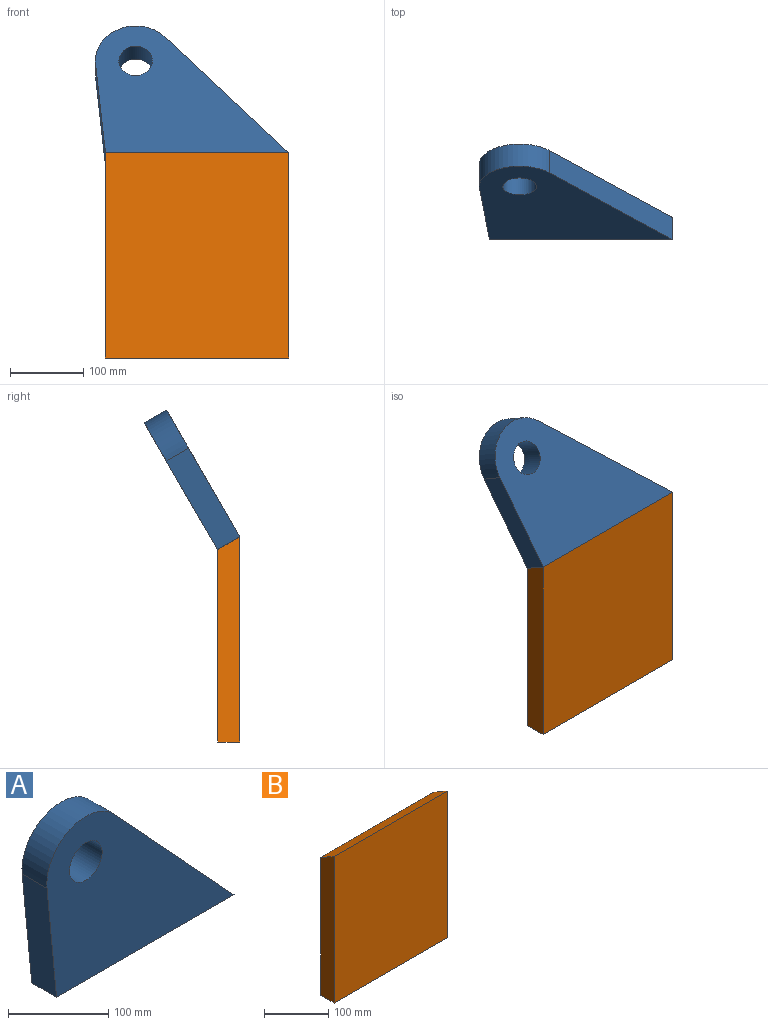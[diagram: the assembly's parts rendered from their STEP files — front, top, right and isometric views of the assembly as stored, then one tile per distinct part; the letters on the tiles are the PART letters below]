
ASSEMBLY  parts=2 mates=1
PART A: 7 faces, bbox 263.7x35x200 mm
  f0: cylinder r=55mm len=95.41mm, axis (0,1,0), area 4797.4mm2, adj f1,f3,f5,f6
  f1: plane 139.73x35mm, normal (-1,0,-0.1), area 4913mm2, adj f0,f2,f5,f6
  f2: plane 250x35mm, normal (0,0,-1), area 8750mm2, adj f1,f3,f5,f6
  f3: plane 182.31x168.3mm, normal (0.73,0,0.68), area 8684.1mm2, adj f0,f2,f5,f6
  f4: cylinder r=23mm len=46mm, axis (0,1,0), area 5058mm2, adj f5,f6
  f5: plane 263.72x200mm, normal (0,-1,0), area 30916mm2, adj f0,f1,f2,f3,f4
  f6: plane 263.72x200mm, normal (0,1,0), area 30916mm2, adj f0,f1,f2,f3,f4
PART B: 6 faces, bbox 250x30x280 mm
  f0: plane 280x30mm, normal (1,0,0), area 8140.2mm2, adj f2,f3,f4,f5
  f1: plane 280x30mm, normal (-1,0,0), area 8140.2mm2, adj f2,f3,f4,f5
  f2: plane 250x30mm, normal (0,0,-1), area 7500mm2, adj f0,f1,f3,f4
  f3: plane 280x250mm, normal (0,-1,0), area 70000mm2, adj f0,f1,f2,f5
  f4: plane 262.68x250mm, normal (0,1,0), area 65669.9mm2, adj f0,f1,f2,f5
  f5: plane 250x30mm, normal (0,0.5,0.87), area 8660.3mm2, adj f0,f1,f3,f4
PLACE A rot(axis=(-1,0,0),30deg) t=(-118.07,-6.87,203.4)mm
PLACE B t=(-118.07,-57.03,-5.79)mm
MATE fastened A.f2 <-> B.f5  axis (0,-0.5,-0.87) through (-118.07,-72.03,125.55)mm
